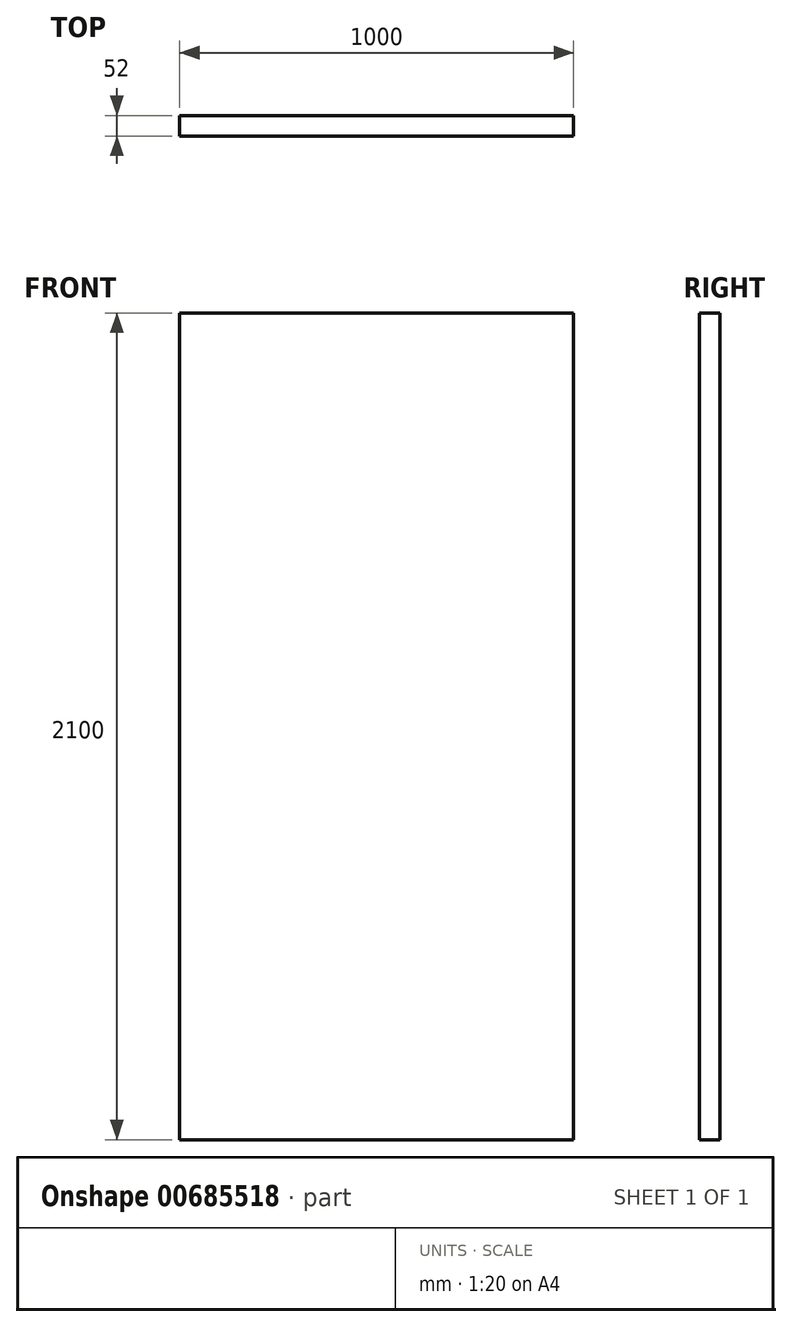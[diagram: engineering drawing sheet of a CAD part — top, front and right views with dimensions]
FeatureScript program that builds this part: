
annotation { "Feature Type Name" : "Feature", "Feature Type Description" : "" }
export const myFeature = defineFeature(function(context is Context, id is Id, definition is map)
    precondition{}
    {
        {
            var Q0;
            Q0=qCreatedBy(makeId("Front.planeOp"),FACE);
            var sketch = newSketch(context, id + "F0", { "sketchPlane" : qUnion([Q0])});
            skLineSegment(sketch, "E0.bottom", {"start": v(3277.39, -1875.66) * mm, "end": v(2277.39, -1875.66) * mm});
            skLineSegment(sketch, "E0.top", {"start": v(3277.39, 224.34) * mm, "end": v(2277.39, 224.34) * mm});
            skLineSegment(sketch, "E0.left", {"start": v(3277.39, -1875.66) * mm, "end": v(3277.39, 224.34) * mm});
            skLineSegment(sketch, "E0.right", {"start": v(2277.39, -1875.66) * mm, "end": v(2277.39, 224.34) * mm});
            skLineSegment(sketch, "E1.bottom", {"start": v(-3545.3, 1839.4) * mm, "end": v(-3330.45, 1839.4) * mm});
            skLineSegment(sketch, "E1.top", {"start": v(-3545.3, 1772.72) * mm, "end": v(-3330.45, 1772.72) * mm});
            skLineSegment(sketch, "E1.left", {"start": v(-3545.3, 1839.4) * mm, "end": v(-3545.3, 1772.72) * mm});
            skLineSegment(sketch, "E1.right", {"start": v(-3330.45, 1839.4) * mm, "end": v(-3330.45, 1772.72) * mm});
            skSolve(sketch);
        }
        {
            var Q0;
            Q0=makeQuery(id+"F0.imprint","IMPRINT",FACE,{"disambiguationData":[TD([[makeQuery(id+"F0.imprint","IMPRINT",EDGE,{"derivedFrom":sQuery(id+"F0.wireOp",EDGE,"E0.bottom")}),-1.0]])]});
            extrude(context, id + "F1", {"entities" : qUnion([Q0]), "depth" : 52 * mm, "offsetDistance" : 25.4 * mm});
        }
    });
